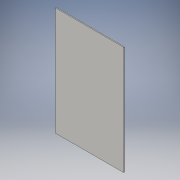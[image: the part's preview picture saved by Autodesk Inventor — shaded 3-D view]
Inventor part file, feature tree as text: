
AUTODESK INVENTOR PART (.ipt)
format: ipt  version: 2016 (Build 200138000, 138)  size: 86,016 bytes
history: native  units: in
note: dims shown in document units (in); Inventor stores cm internally (conversion verified against a paired STEP export)
features: extrude x1, sketch x1
ambient origin geometry x8: Origin, YZ Plane, XZ Plane, XY Plane, X Axis, Y Axis, Z Axis, Center Point
bodies: Solid1 (feature_tree)
feature tree (2):
  extrude  "Extrusion1"  Depth=15.086in
  sketch  "Sketch1"  dims[d0=9.5in d1=15.086in d2=0.125in d3=0.0in]
